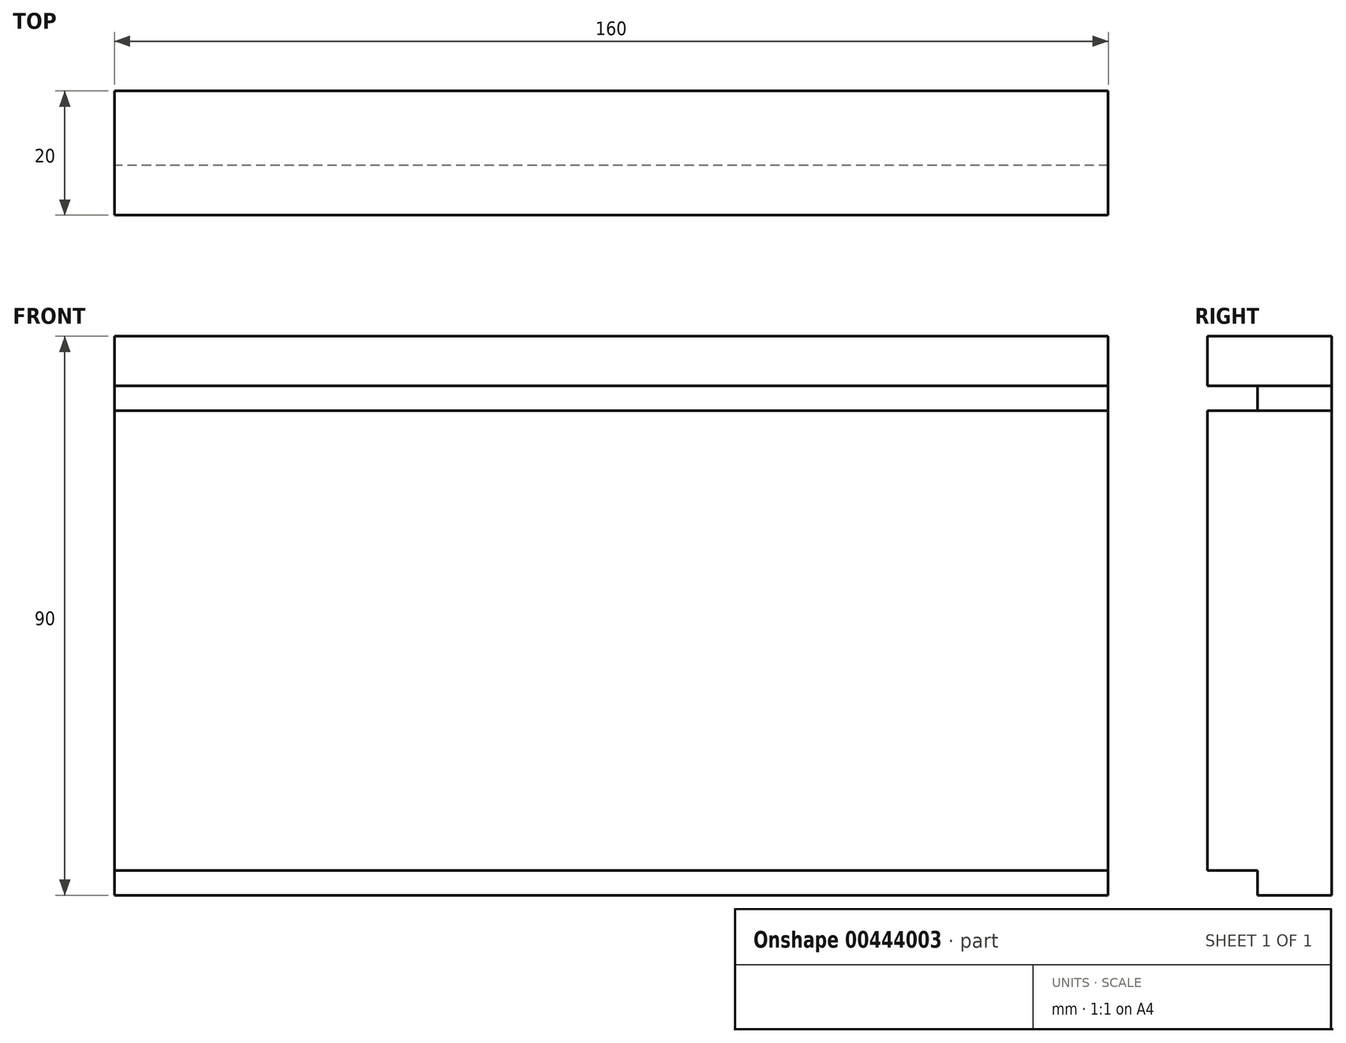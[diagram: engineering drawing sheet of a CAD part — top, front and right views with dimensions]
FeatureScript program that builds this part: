
annotation { "Feature Type Name" : "Feature", "Feature Type Description" : "" }
export const myFeature = defineFeature(function(context is Context, id is Id, definition is map)
    precondition{}
    {
        {
            var Q0;
            Q0=qCreatedBy(makeId("Front.planeOp"),FACE);
            var sketch = newSketch(context, id + "F0", { "sketchPlane" : qUnion([Q0])});
            skLineSegment(sketch, "E0.bottom", {"start": v(82.15, 47.23) * mm, "end": v(-77.85, 47.23) * mm});
            skLineSegment(sketch, "E0.top", {"start": v(82.15, -42.77) * mm, "end": v(-77.85, -42.77) * mm});
            skLineSegment(sketch, "E0.left", {"start": v(82.15, 47.23) * mm, "end": v(82.15, -42.77) * mm});
            skLineSegment(sketch, "E0.right", {"start": v(-77.85, 47.23) * mm, "end": v(-77.85, -42.77) * mm});
            skLineSegment(sketch, "E1", {"start": v(82.15, -38.77) * mm, "end": v(-77.85, -38.77) * mm});
            skLineSegment(sketch, "E2", {"start": v(82.15, 39.23) * mm, "end": v(-77.85, 39.23) * mm});
            skLineSegment(sketch, "E3", {"start": v(82.15, 35.23) * mm, "end": v(-77.85, 35.23) * mm});
            skSolve(sketch);
        }
        {
            var Q0;
            {var subQ0=sQuery(id+"F0.wireOp",EDGE,"E1");Q0=makeQuery(id+"F0.imprint","IMPRINT",FACE,{"disambiguationData":[TD([[makeQuery(id+"F0.imprint","IMPRINT",EDGE,{"derivedFrom":subQ0}),-1.0]])]});}
            extrude(context, id + "F1", {"entities" : qUnion([Q0]), "depth" : 20 * mm});
        }
        {
            var Q0;
            {var subQ0=sQuery(id+"F0.wireOp",EDGE,"E0.bottom");Q0=makeQuery(id+"F0.imprint","IMPRINT",FACE,{"disambiguationData":[TD([[makeQuery(id+"F0.imprint","IMPRINT",EDGE,{"derivedFrom":subQ0}),1.0]])]});}
            extrude(context, id + "F2", {"entities" : qUnion([Q0]), "depth" : 20 * mm});
        }
        {
            var Q0;
            {var subQ0=sQuery(id+"F0.wireOp",EDGE,"E2");Q0=makeQuery(id+"F0.imprint","IMPRINT",FACE,{"disambiguationData":[TD([[makeQuery(id+"F0.imprint","IMPRINT",EDGE,{"derivedFrom":subQ0}),1.0]])]});}
            extrude(context, id + "F3", {"entities" : qUnion([Q0]), "depth" : 12 * mm});
        }
        {
            var Q0;
            {var subQ0=sQuery(id+"F0.wireOp",EDGE,"E0.top");Q0=makeQuery(id+"F0.imprint","IMPRINT",FACE,{"disambiguationData":[TD([[makeQuery(id+"F0.imprint","IMPRINT",EDGE,{"derivedFrom":subQ0}),-1.0]])]});}
            extrude(context, id + "F4", {"entities" : qUnion([Q0]), "operationType" : NewBodyOperationType.ADD, "depth" : 12 * mm});
        }
    });
